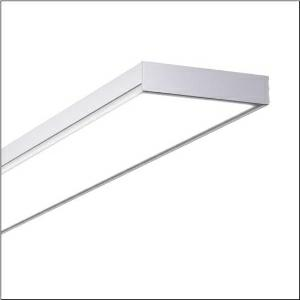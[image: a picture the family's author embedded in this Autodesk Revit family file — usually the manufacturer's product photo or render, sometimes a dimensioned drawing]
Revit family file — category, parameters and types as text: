
# Revit family: apollon_r__31_surface_51mp26wm2341e_8ded
name_source: partatom
category: Lighting Fixtures
units: mm (PartAtom-declared; Revit-internal decimal feet)

## family parameters
Cut with Voids When Loaded = No
Host = Face
Light Source = No
Part Type = Normal
Room Calculation Point = No
Round Connector Dimension = Use Diameter
Shared = No

## types (1)
- Apollon® 31 Surface (1 x LED, 4400 lm, 33 W, 3000K)
    Apparent Load = 33 VA
    CIE Flux Codes = 61 87 97 97 100
    Color Rendering = 80
    Color Temperature = 3000K
    Default Elevation = 1800 mm
    Description = Apollon® 31 Surface, office luminaire, primary optical cover: micro prismatic cover, of PMMA, light emission: direct distribution, primary light characteristic: symmetric, installation type: surface-mounted, LED, rated luminous flux: 4.400lm, luminous efficacy: 133lm/W, light colour: 830, colour temperature: 3000K, control gear: ON/OFF Multilumen, with terminal, 3-pole, mains connection: 220..240V, AC, 50/60Hz, rated input power: 33W, housing, of sheet steel, coil coated, metallic grey (RAL 9006), length: 1.545mm, width: 200mm, height: 44mm, protection rating (complete): IP20, insulation class (complete): insulation class II (safety insulation), certification: CE, impact resistance: IK02, permissible operating ambient temperature: -20..+40°C, packaging unit: 1 piece
    Height = 44 mm
    Lamp = 1 x LED
    Lamp Light Flux = 4400 lm
    Lamp Power = 33 W
    Lamp count = 1
    Length = 1545 mm
    Luminous efficacy = 133 lm/W
    Manufacturer = Siteco
    ModVariant = No
    Model = 51MP26WM2341E
    Mounting Place = Ceiling
    Mounting Type = Surface mounted
    Number of Poles = 1
    OnlyDefault = Yes
    Power Factor = 1
    Product Name = Apollon® 31 Surface
    Product group = office luminaire | ceiling mounted
    ProductGroupID = 302
    Protection Class = Protection class II
    Protection Degree = IP 20
    RLX_Detail_Level = 1
    RLX_Emergency_Light_Flux = 0 lm
    RLX_Emergency_Type = 0
    RLX_Emergency_Type_DB = No
    RlxData = <blob elided: 24081 chars, md5=ca13e680>
    Socket = socket
    Standby Power = 0 W
    System Light Flux = 4400 lm
    System Power = 33 W
    Type Comments = Product without accessories
    Type Image = l_1313654.jpg
    URL = http://relux.com
    VarID = ---
    Voltage = 0 V
    Weight = 0.00 kg
    Width = 200 mm  [stored 0.656168 ft]

note: [stored X ft] marks values corroborated as IEEE doubles in the binary element streams (Revit-internal decimal feet)

## geometry (parser evidence)
native form markers: Blend x4, Sweep x10
no freeform markers — native parametric forms only
